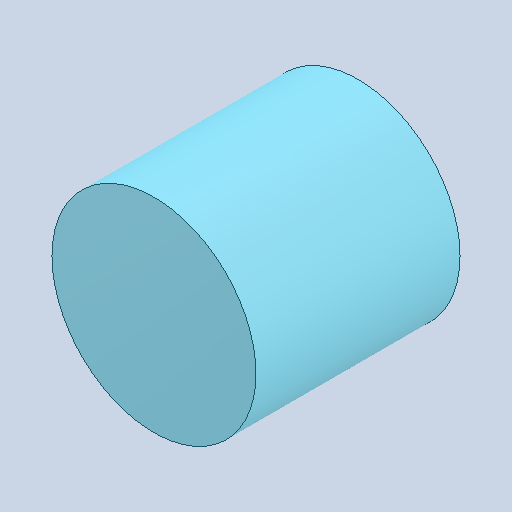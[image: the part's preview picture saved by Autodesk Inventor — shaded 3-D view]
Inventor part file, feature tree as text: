
AUTODESK INVENTOR PART (.ipt)
format: ipt  version: 2022 (Build 260153000, 153)  size: 95,232 bytes
history: imported  units: in
note: dims shown in document units (in); Inventor stores cm internally (conversion verified against a paired STEP export)
features: imported_body x1
ambient origin geometry x8: Origin, YZ Plane, XZ Plane, XY Plane, X Axis, Y Axis, Z Axis, Center Point
bodies: Solid1 (imported_parasolid), Body1 (imported_parasolid)
feature tree (1):
  imported_body  NMx_Import_Brep_tag  [imported B-rep: ~3 faces, bbox_mm=[0.0, 0.0, 6.35]]
